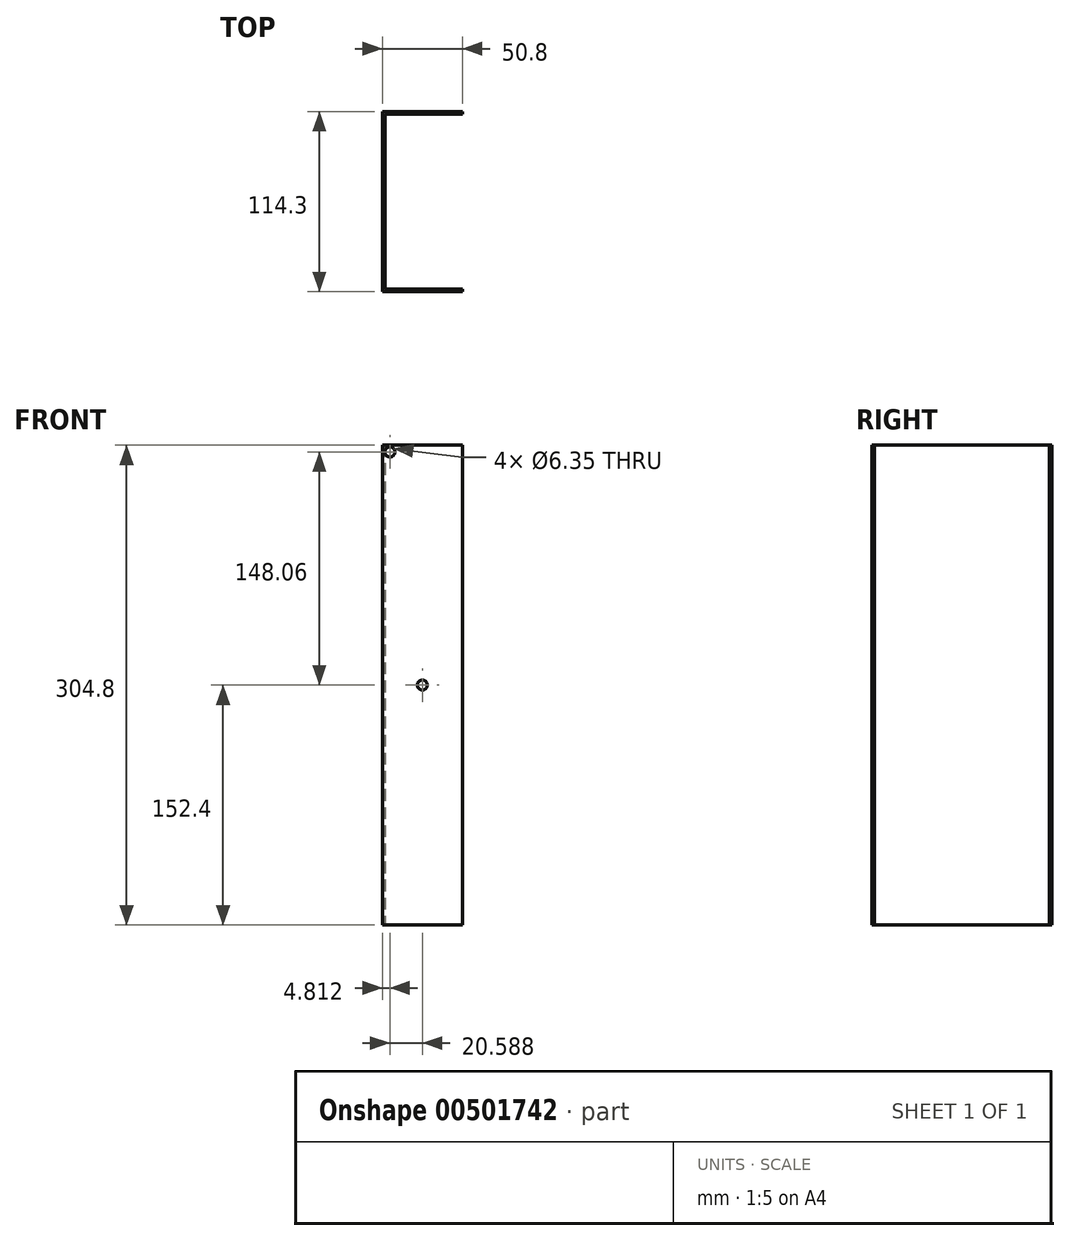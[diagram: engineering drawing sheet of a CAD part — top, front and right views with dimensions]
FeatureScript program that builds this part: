
annotation { "Feature Type Name" : "Feature", "Feature Type Description" : "" }
export const myFeature = defineFeature(function(context is Context, id is Id, definition is map)
    precondition{}
    {
        {
            var Q0;
            Q0=qCreatedBy(makeId("Front.planeOp"),FACE);
            var sketch = newSketch(context, id + "F0", { "sketchPlane" : qUnion([Q0])});
            skLineSegment(sketch, "E0.bottom", {"start": v(25.4, -152.4) * mm, "end": v(-25.4, -152.4) * mm});
            skLineSegment(sketch, "E0.top", {"start": v(25.4, 152.4) * mm, "end": v(-25.4, 152.4) * mm});
            skLineSegment(sketch, "E0.left", {"start": v(25.4, -152.4) * mm, "end": v(25.4, 152.4) * mm});
            skLineSegment(sketch, "E0.right", {"start": v(-25.4, -152.4) * mm, "end": v(-25.4, 152.4) * mm});
            skPoint(sketch, "E0.middle", {"position": v(0, 0) * mm});
            skSolve(sketch);
        }
        {
            var Q0;
            Q0 = qSketchRegion(id + "F0", true);
            extrude(context, id + "F1", {"entities" : qUnion([Q0]), "oppositeDirection" : true, "depth" : 1.59 * mm});
        }
        {
            var Q0;
            Q0=makeQuery(id+"F1.opExtrude","SWEPT_FACE",FACE,{"disambiguationData":[OSD([sQuery(id+"F0.wireOp",EDGE,"E0.right")])]});
            var sketch = newSketch(context, id + "F2", { "sketchPlane" : qUnion([Q0])});
            skLineSegment(sketch, "E1", {"start": v(0, -152.4) * mm, "end": v(-114.3, -152.4) * mm});
            skLineSegment(sketch, "E2", {"start": v(0, 152.4) * mm, "end": v(-114.3, 152.4) * mm});
            skLineSegment(sketch, "E3", {"start": v(-114.3, 152.4) * mm, "end": v(-114.3, -152.4) * mm});
            skLineSegment(sketch, "E4", {"start": v(0, -152.4) * mm, "end": v(0, 152.4) * mm});
            skSolve(sketch);
        }
        {
            var Q0;
            Q0 = qSketchRegion(id + "F2", true);
            extrude(context, id + "F3", {"entities" : qUnion([Q0]), "operationType" : NewBodyOperationType.ADD, "oppositeDirection" : true, "depth" : 1.59 * mm});
        }
        {
            var Q0;
            Q0=makeQuery(id+"F3.opExtrude","SWEPT_FACE",FACE,{"disambiguationData":[OSD([sQuery(id+"F2.wireOp",EDGE,"E3")])]});
            var sketch = newSketch(context, id + "F4", { "sketchPlane" : qUnion([Q0])});
            skLineSegment(sketch, "E5", {"start": v(25.4, 152.4) * mm, "end": v(-25.4, 152.4) * mm});
            skLineSegment(sketch, "E6", {"start": v(25.4, -152.4) * mm, "end": v(-25.4, -152.4) * mm});
            skLineSegment(sketch, "E7", {"start": v(-25.4, -152.4) * mm, "end": v(-25.4, 152.4) * mm});
            skLineSegment(sketch, "E8", {"start": v(25.4, 152.4) * mm, "end": v(25.4, -152.4) * mm});
            skSolve(sketch);
        }
        {
            var Q0;
            Q0 = qSketchRegion(id + "F4", true);
            extrude(context, id + "F5", {"entities" : qUnion([Q0]), "operationType" : NewBodyOperationType.ADD, "oppositeDirection" : true, "depth" : 1.59 * mm});
        }
        {
            var Q0;
            Q0=makeQuery(id+"F5.boolean.opBoolean","MERGE",FACE,{"derivedFrom":[makeQuery(id+"F3.opExtrude","SWEPT_FACE",FACE,{"disambiguationData":[OSD([sQuery(id+"F2.wireOp",EDGE,"E3")])]}),makeQuery(id+"F5.opExtrude","CAP_FACE",FACE,{"disambiguationData":[OSD([sQuery(id+"F4.wireOp",EDGE,"E5"),sQuery(id+"F4.wireOp",EDGE,"E6"),sQuery(id+"F4.wireOp",EDGE,"E7"),sQuery(id+"F4.wireOp",EDGE,"E8")])],"isStart":true})]});
            var sketch = newSketch(context, id + "F6", { "sketchPlane" : qUnion([Q0])});
            skCircle(sketch, "E9", {"center": v(20.59, 148.06) * mm, "radius": 3.18 * mm});
            skSolve(sketch);
        }
        {
            var Q0;
            Q0 = qSketchRegion(id + "F6", true);
            extrude(context, id + "F7", {"entities" : qUnion([Q0]), "operationType" : NewBodyOperationType.REMOVE, "oppositeDirection" : true, "depth" : 136.9 * mm});
        }
        {
            var Q0;
            Q0=makeQuery(id+"F1.opExtrude","CAP_FACE",FACE,{"disambiguationData":[OSD([sQuery(id+"F0.wireOp",EDGE,"E0.bottom"),sQuery(id+"F0.wireOp",EDGE,"E0.top"),sQuery(id+"F0.wireOp",EDGE,"E0.left"),sQuery(id+"F0.wireOp",EDGE,"E0.right")])],"isStart":true});
            var sketch = newSketch(context, id + "F8", { "sketchPlane" : qUnion([Q0])});
            skCircle(sketch, "E10", {"center": v(0, 0) * mm, "radius": 3.18 * mm});
            skSolve(sketch);
        }
        {
            var Q0;
            Q0 = qSketchRegion(id + "F8", true);
            extrude(context, id + "F9", {"entities" : qUnion([Q0]), "operationType" : NewBodyOperationType.REMOVE, "oppositeDirection" : true, "depth" : 146.3 * mm});
        }
    });
